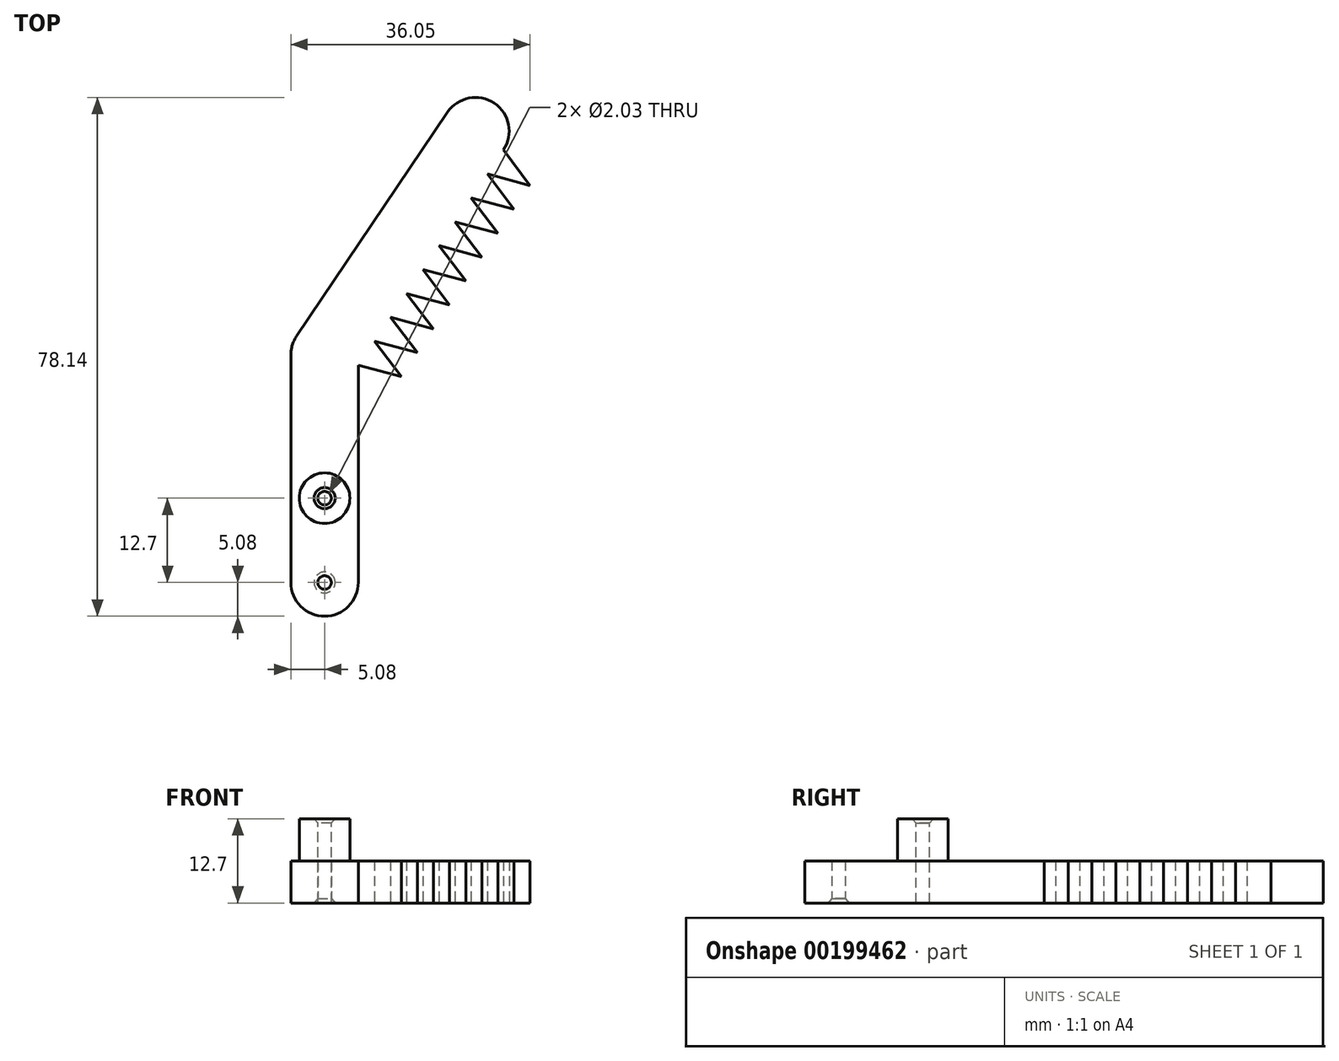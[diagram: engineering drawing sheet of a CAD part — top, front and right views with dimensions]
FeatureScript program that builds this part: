
annotation { "Feature Type Name" : "Feature", "Feature Type Description" : "" }
export const myFeature = defineFeature(function(context is Context, id is Id, definition is map)
    precondition{}
    {
        {
            var Q0;
            Q0=qCreatedBy(makeId("Top.planeOp"),FACE);
            var sketch = newSketch(context, id + "F0", { "sketchPlane" : qUnion([Q0])});
            skLineSegment(sketch, "E0", {"start": v(0, 0) * mm, "end": v(0, 12.7) * mm});
            skLineSegment(sketch, "E1", {"start": v(0, 12.7) * mm, "end": v(0, 34.29) * mm});
            skLineSegment(sketch, "E2", {"start": v(0, 34.3) * mm, "end": v(22.73, 67.98) * mm});
            skArc(sketch, "E3.0.startCap", {"start": v(4.21, 31.45) * mm, "mid": v(-2.84, 30.08) * mm, "end": v(-4.21, 37.13) * mm});
            skArc(sketch, "E3.0.endCap", {"start": v(18.51, 70.82) * mm, "mid": v(25.57, 72.2) * mm, "end": v(26.94, 65.14) * mm});
            skLineSegment(sketch, "E3.0.left", {"start": v(-4.21, 37.13) * mm, "end": v(18.51, 70.82) * mm});
            skLineSegment(sketch, "E3.0.right", {"start": v(4.21, 31.45) * mm, "end": v(26.94, 65.14) * mm});
            skArc(sketch, "E3.1.startCap", {"start": v(5.08, 12.7) * mm, "mid": v(0, 7.62) * mm, "end": v(-5.08, 12.7) * mm});
            skArc(sketch, "E3.1.endCap", {"start": v(-5.08, 34.29) * mm, "mid": v(0, 39.37) * mm, "end": v(5.08, 34.29) * mm});
            skLineSegment(sketch, "E3.1.left", {"start": v(-5.08, 12.7) * mm, "end": v(-5.08, 34.29) * mm});
            skLineSegment(sketch, "E3.1.right", {"start": v(5.08, 12.7) * mm, "end": v(5.08, 34.29) * mm});
            skArc(sketch, "E3.2.startCap", {"start": v(5.08, 0) * mm, "mid": v(0, -5.08) * mm, "end": v(-5.08, 0) * mm});
            skArc(sketch, "E3.2.endCap", {"start": v(-5.08, 12.7) * mm, "mid": v(0, 17.78) * mm, "end": v(5.08, 12.7) * mm});
            skLineSegment(sketch, "E3.2.left", {"start": v(-5.08, 0) * mm, "end": v(-5.08, 12.7) * mm});
            skLineSegment(sketch, "E3.2.right", {"start": v(5.08, 0) * mm, "end": v(5.08, 12.7) * mm});
            skPoint(sketch, "E4", {"position": v(5.08, 32.74) * mm});
            skLineSegment(sketch, "E5", {"start": v(5.08, 32.74) * mm, "end": v(10.34, 29.19) * mm});
            skLineSegment(sketch, "E6", {"start": v(5.08, 32.74) * mm, "end": v(7.5, 36.34) * mm});
            skLineSegment(sketch, "E7", {"start": v(7.5, 36.34) * mm, "end": v(9.94, 39.94) * mm});
            skLineSegment(sketch, "E8", {"start": v(9.94, 39.94) * mm, "end": v(12.37, 43.54) * mm});
            skLineSegment(sketch, "E9", {"start": v(12.37, 43.54) * mm, "end": v(14.8, 47.14) * mm});
            skLineSegment(sketch, "E10", {"start": v(15.57, 48.3) * mm, "end": v(17.22, 50.74) * mm});
            skLineSegment(sketch, "E11", {"start": v(17.22, 50.74) * mm, "end": v(19.65, 54.34) * mm});
            skLineSegment(sketch, "E12", {"start": v(19.65, 54.34) * mm, "end": v(22.08, 57.94) * mm});
            skLineSegment(sketch, "E13", {"start": v(22.08, 57.94) * mm, "end": v(24.5, 61.54) * mm});
            skLineSegment(sketch, "E14", {"start": v(24.5, 61.54) * mm, "end": v(26.94, 65.14) * mm});
            skLineSegment(sketch, "E15", {"start": v(10.34, 29.19) * mm, "end": v(32.18, 61.6) * mm, "construction": true});
            skLineSegment(sketch, "E16", {"start": v(26.94, 65.14) * mm, "end": v(32.18, 61.6) * mm});
            skLineSegment(sketch, "E17", {"start": v(5.08, 32.74) * mm, "end": v(11.56, 30.99) * mm});
            skLineSegment(sketch, "E18", {"start": v(11.56, 30.99) * mm, "end": v(7.5, 36.34) * mm});
            skLineSegment(sketch, "E19", {"start": v(7.5, 36.34) * mm, "end": v(13.99, 34.6) * mm});
            skLineSegment(sketch, "E20", {"start": v(13.99, 34.6) * mm, "end": v(9.94, 39.94) * mm});
            skLineSegment(sketch, "E21", {"start": v(9.94, 39.94) * mm, "end": v(16.41, 38.2) * mm});
            skLineSegment(sketch, "E22", {"start": v(16.41, 38.2) * mm, "end": v(12.37, 43.54) * mm});
            skLineSegment(sketch, "E23", {"start": v(14.8, 47.14) * mm, "end": v(18.84, 41.8) * mm});
            skLineSegment(sketch, "E24", {"start": v(18.84, 41.8) * mm, "end": v(12.37, 43.54) * mm});
            skLineSegment(sketch, "E25", {"start": v(14.8, 47.14) * mm, "end": v(21.26, 45.4) * mm});
            skLineSegment(sketch, "E26", {"start": v(21.26, 45.4) * mm, "end": v(17.22, 50.74) * mm});
            skLineSegment(sketch, "E27", {"start": v(17.22, 50.74) * mm, "end": v(23.69, 49) * mm});
            skLineSegment(sketch, "E28", {"start": v(23.69, 49) * mm, "end": v(19.65, 54.34) * mm});
            skLineSegment(sketch, "E29", {"start": v(22.08, 57.94) * mm, "end": v(26.11, 52.6) * mm});
            skLineSegment(sketch, "E30", {"start": v(26.11, 52.6) * mm, "end": v(19.65, 54.34) * mm});
            skLineSegment(sketch, "E31", {"start": v(24.5, 61.54) * mm, "end": v(28.54, 56.2) * mm});
            skLineSegment(sketch, "E32", {"start": v(28.54, 56.2) * mm, "end": v(22.08, 57.94) * mm});
            skLineSegment(sketch, "E33", {"start": v(26.94, 65.14) * mm, "end": v(30.97, 59.8) * mm});
            skLineSegment(sketch, "E34", {"start": v(30.97, 59.8) * mm, "end": v(24.5, 61.54) * mm});
            skSolve(sketch);
        }
        {
            var Q0;
            Q0 = qSketchRegion(id + "F0", true);
            extrude(context, id + "F1", {"entities" : qUnion([Q0]), "depth" : 6.35 * mm});
        }
        {
            var Q0;
            Q0=makeQuery(id+"F1.opExtrude","CAP_FACE",FACE,{"disambiguationData":[OSD([sQuery(id+"F0.wireOp",EDGE,"E3.0.endCap"),sQuery(id+"F0.wireOp",EDGE,"E3.0.left"),sQuery(id+"F0.wireOp",EDGE,"E3.0.right"),sQuery(id+"F0.wireOp",EDGE,"E3.1.endCap"),sQuery(id+"F0.wireOp",EDGE,"E3.1.left"),sQuery(id+"F0.wireOp",EDGE,"E3.1.right"),sQuery(id+"F0.wireOp",EDGE,"E3.2.startCap"),sQuery(id+"F0.wireOp",EDGE,"E3.2.left"),sQuery(id+"F0.wireOp",EDGE,"E3.2.right")])],"isStart":false});
            var sketch = newSketch(context, id + "F2", { "sketchPlane" : qUnion([Q0])});
            skCircle(sketch, "E35", {"center": v(0, 12.7) * mm, "radius": 3.81 * mm});
            skSolve(sketch);
        }
        {
            var Q0;
            Q0 = qSketchRegion(id + "F2", true);
            extrude(context, id + "F3", {"entities" : qUnion([Q0]), "operationType" : NewBodyOperationType.ADD, "depth" : 6.35 * mm});
        }
        {
            var Q0;
            Q0=makeQuery(id+"F3.opExtrude","CAP_FACE",FACE,{"disambiguationData":[OSD([sQuery(id+"F2.wireOp",EDGE,"E35")])],"isStart":false});
            var sketch = newSketch(context, id + "F4", { "sketchPlane" : qUnion([Q0])});
            skPoint(sketch, "E36", {"position": v(0, 12.7) * mm});
            skSolve(sketch);
        }
        {
            var Q0;
            Q0=sQuery(id+"F4.wireOp",VERTEX,"E36");
            var Q1;
            Q1=makeQuery(id+"F1.opExtrude","SWEPT_BODY",BODY,{"disambiguationData":[OSD([sQuery(id+"F0.wireOp",EDGE,"E3.0.endCap"),sQuery(id+"F0.wireOp",EDGE,"E3.0.left"),sQuery(id+"F0.wireOp",EDGE,"E3.0.right"),sQuery(id+"F0.wireOp",EDGE,"E3.1.endCap"),sQuery(id+"F0.wireOp",EDGE,"E3.1.left"),sQuery(id+"F0.wireOp",EDGE,"E3.1.right"),sQuery(id+"F0.wireOp",EDGE,"E3.2.startCap"),sQuery(id+"F0.wireOp",EDGE,"E3.2.left"),sQuery(id+"F0.wireOp",EDGE,"E3.2.right")])]});
            hole(context, id + "F5", {"style" : HoleStyle.C_SINK, "endStyle" : HoleEndStyle.THROUGH, "holeDiameter" : 2.03 * mm, "cSinkDiameter" : 3.17 * mm, "cSinkAngle" : 82 * degree, "locations" : qUnion([Q0]), "scope" : qUnion([Q1]), "isTappedThrough" : true});
        }
        {
            var Q0;
            Q0=sQuery(id+"F0.wireOp",VERTEX,"E3.2.startCap.center");
            var Q1;
            Q1=makeQuery(id+"F1.opExtrude","SWEPT_BODY",BODY,{"disambiguationData":[OSD([sQuery(id+"F0.wireOp",EDGE,"E3.0.endCap"),sQuery(id+"F0.wireOp",EDGE,"E3.0.left"),sQuery(id+"F0.wireOp",EDGE,"E3.0.right"),sQuery(id+"F0.wireOp",EDGE,"E3.1.endCap"),sQuery(id+"F0.wireOp",EDGE,"E3.1.left"),sQuery(id+"F0.wireOp",EDGE,"E3.1.right"),sQuery(id+"F0.wireOp",EDGE,"E3.2.startCap"),sQuery(id+"F0.wireOp",EDGE,"E3.2.left"),sQuery(id+"F0.wireOp",EDGE,"E3.2.right")])]});
            hole(context, id + "F6", {"style" : HoleStyle.C_SINK, "endStyle" : HoleEndStyle.THROUGH, "oppositeDirection" : true, "holeDiameter" : 2.03 * mm, "cSinkDiameter" : 3.17 * mm, "cSinkAngle" : 82 * degree, "locations" : qUnion([Q0]), "scope" : qUnion([Q1]), "isTappedThrough" : true});
        }
    });
